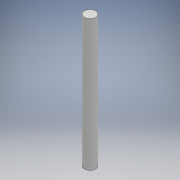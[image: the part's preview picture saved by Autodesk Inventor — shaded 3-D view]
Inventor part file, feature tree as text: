
AUTODESK INVENTOR PART (.ipt)
format: ipt  version: 2018 (Build 220112000, 112)  size: 89,088 bytes
history: native  units: mm
features: extrude x1, sketch x1
ambient origin geometry x8: Origin, YZ Plane, XZ Plane, XY Plane, X Axis, Y Axis, Z Axis, Center Point
bodies: Solid1 (feature_tree)
feature tree (2):
  extrude  "Extrusion1"  Depth=820.0mm TaperAngle=0.0deg
  sketch  "Sketch1"  dims[d0=70.0mm d1=820.0mm d2=0.0mm]
